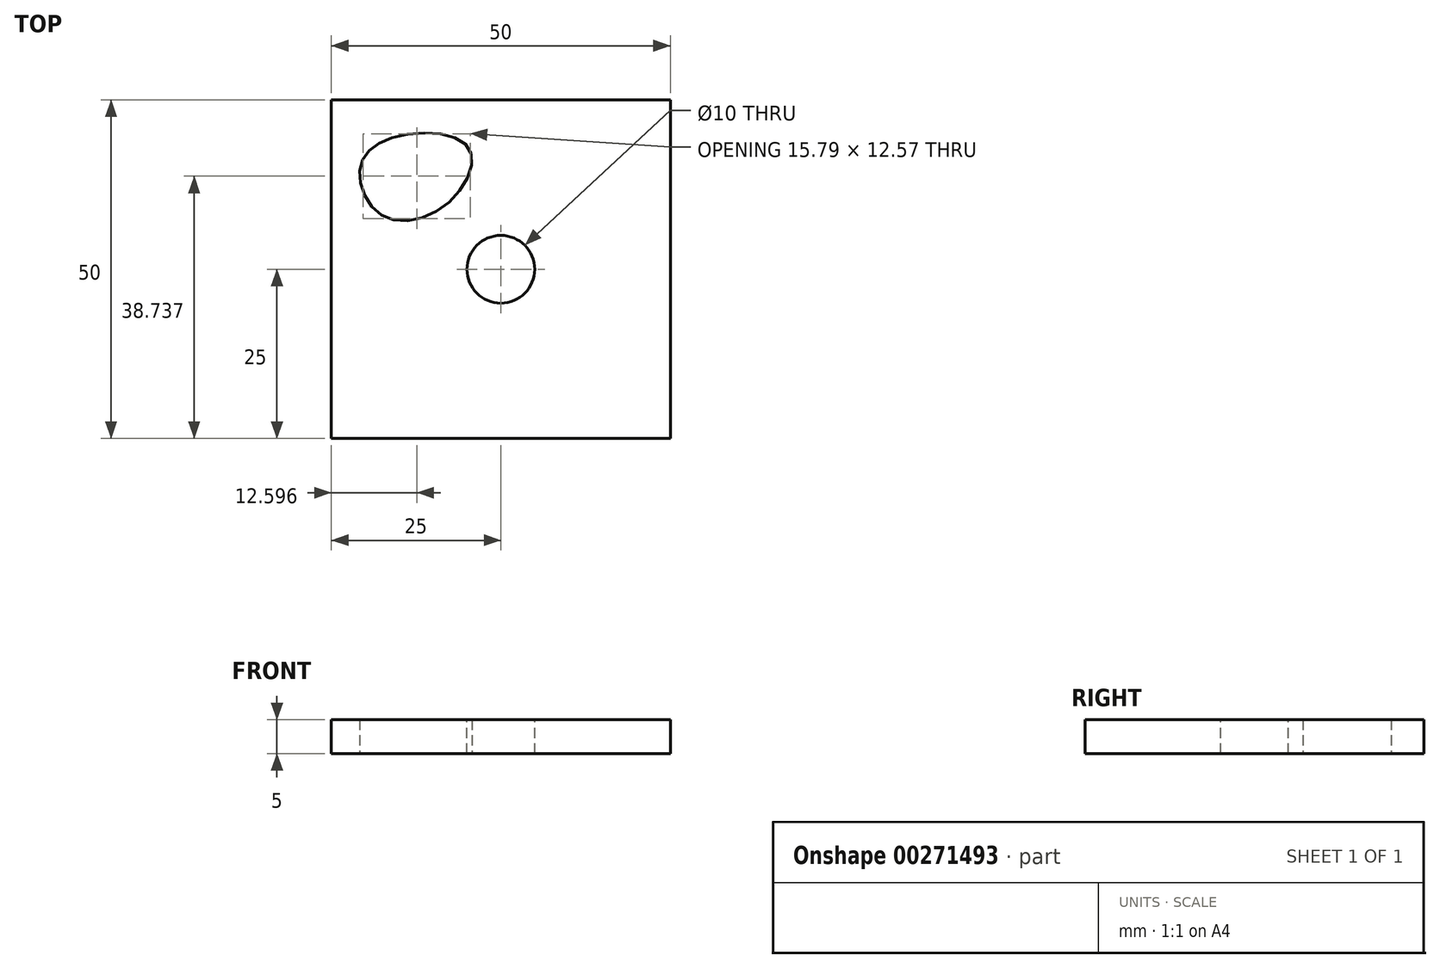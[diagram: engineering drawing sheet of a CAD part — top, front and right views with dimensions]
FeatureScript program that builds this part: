
annotation { "Feature Type Name" : "Feature", "Feature Type Description" : "" }
export const myFeature = defineFeature(function(context is Context, id is Id, definition is map)
    precondition{}
    {
        {
            var Q0;
            Q0=qCreatedBy(makeId("Top.planeOp"),FACE);
            var sketch = newSketch(context, id + "F0", { "sketchPlane" : qUnion([Q0])});
            skLineSegment(sketch, "E0.bottom", {"start": v(-25, 25) * mm, "end": v(25, 25) * mm});
            skLineSegment(sketch, "E0.top", {"start": v(-25, -25) * mm, "end": v(25, -25) * mm});
            skLineSegment(sketch, "E0.left", {"start": v(-25, 25) * mm, "end": v(-25, -25) * mm});
            skLineSegment(sketch, "E0.right", {"start": v(25, 25) * mm, "end": v(25, -25) * mm});
            skPoint(sketch, "E0.middle", {"position": v(0, 0) * mm});
            skSolve(sketch);
        }
        {
            var Q0;
            Q0=makeQuery(id+"F0.imprint","IMPRINT",FACE,{"disambiguationData":[TD([[makeQuery(id+"F0.imprint","IMPRINT",EDGE,{"derivedFrom":sQuery(id+"F0.wireOp",EDGE,"E0.bottom")}),-1.0]])]});
            extrude(context, id + "F1", {"entities" : qUnion([Q0]), "depth" : 5 * mm});
        }
        {
            var Q0;
            Q0=makeQuery(id+"F1.opExtrude","CAP_FACE",FACE,{"disambiguationData":[OSD([sQuery(id+"F0.wireOp",EDGE,"E0.bottom"),sQuery(id+"F0.wireOp",EDGE,"E0.top"),sQuery(id+"F0.wireOp",EDGE,"E0.left"),sQuery(id+"F0.wireOp",EDGE,"E0.right")])],"isStart":false});
            var sketch = newSketch(context, id + "F2", { "sketchPlane" : qUnion([Q0])});
            skCircle(sketch, "E1", {"center": v(0, 0) * mm, "radius": 5 * mm});
            skSolve(sketch);
        }
        {
            var Q0;
            Q0=makeQuery(id+"F2.imprint","IMPRINT",FACE,{"disambiguationData":[TD([[makeQuery(id+"F2.imprint","IMPRINT",EDGE,{"derivedFrom":sQuery(id+"F2.wireOp",EDGE,"E1")}),1.0]])]});
            extrude(context, id + "F3", {"entities" : qUnion([Q0]), "operationType" : NewBodyOperationType.REMOVE, "oppositeDirection" : true, "depth" : 25 * mm});
        }
        {
            var Q0;
            Q0=makeQuery(id+"F1.opExtrude","CAP_FACE",FACE,{"disambiguationData":[OSD([sQuery(id+"F0.wireOp",EDGE,"E0.bottom"),sQuery(id+"F0.wireOp",EDGE,"E0.top"),sQuery(id+"F0.wireOp",EDGE,"E0.left"),sQuery(id+"F0.wireOp",EDGE,"E0.right")])],"isStart":false});
            var sketch = newSketch(context, id + "F4", { "sketchPlane" : qUnion([Q0])});
            skFitSpline(sketch, "E2", {"points": [v(-16.1, 19.4) * mm, v(-4.97, 18.22) * mm, v(-6.86, 10.65) * mm, v(-16.8, 7.57) * mm, v(-20.83, 14.44) * mm, v(-16.1, 19.4) * mm]});
            skSolve(sketch);
        }
        {
            var Q0;
            Q0=makeQuery(id+"F4.imprint","IMPRINT",FACE,{"disambiguationData":[TD([[makeQuery(id+"F4.imprint","IMPRINT",EDGE,{"derivedFrom":sQuery(id+"F4.wireOp",EDGE,"E2")}),-1.0]])]});
            extrude(context, id + "F5", {"entities" : qUnion([Q0]), "operationType" : NewBodyOperationType.REMOVE, "oppositeDirection" : true, "depth" : 25 * mm});
        }
    });
